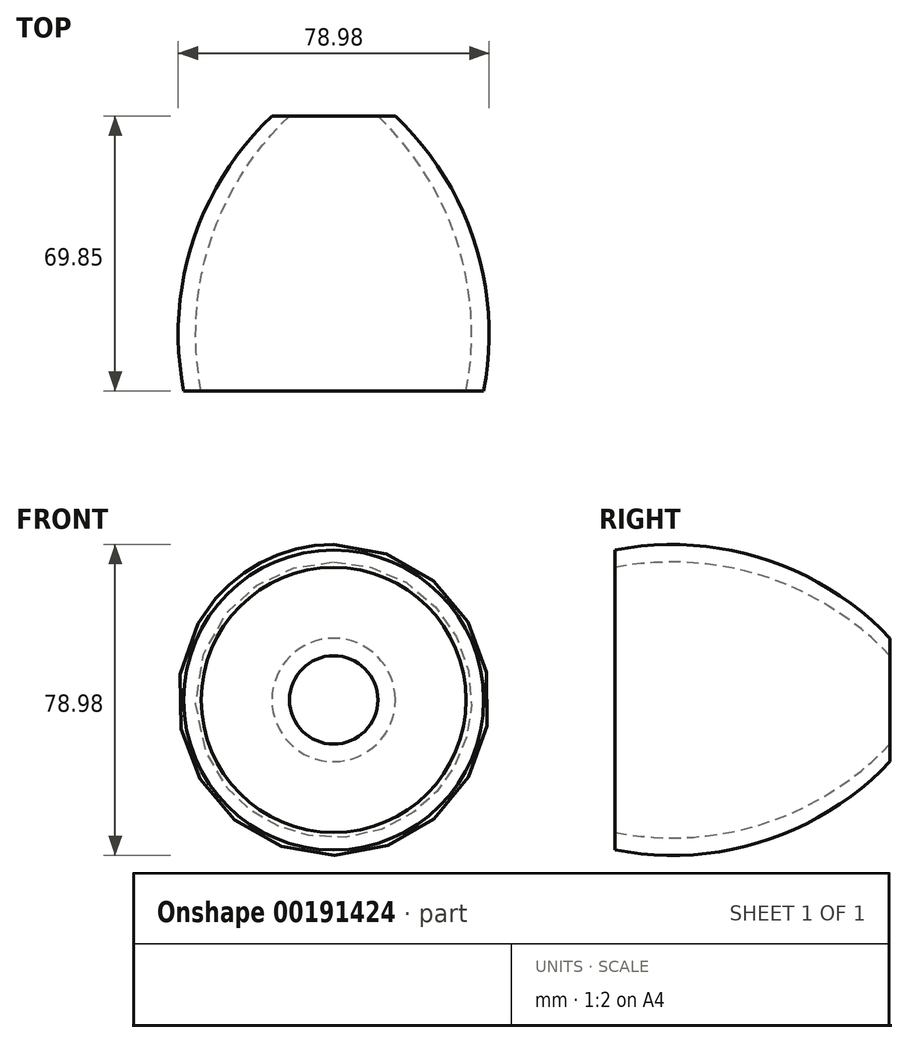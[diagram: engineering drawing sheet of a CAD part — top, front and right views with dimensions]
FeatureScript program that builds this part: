
annotation { "Feature Type Name" : "Feature", "Feature Type Description" : "" }
export const myFeature = defineFeature(function(context is Context, id is Id, definition is map)
    precondition{}
    {
        {
            var Q0;
            Q0=qCreatedBy(makeId("Top.planeOp"),FACE);
            var sketch = newSketch(context, id + "F0", { "sketchPlane" : qUnion([Q0])});
            skLineSegment(sketch, "E0", {"start": v(0, 0) * mm, "end": v(-38.1, 0) * mm});
            skArc(sketch, "E1", {"start": v(0, 81.28) * mm, "mid": v(-32.29, 46.85) * mm, "end": v(-38.1, 0) * mm});
            skLineSegment(sketch, "E2", {"start": v(0, 81.28) * mm, "end": v(0, 0) * mm});
            skLineSegment(sketch, "E3", {"start": v(0, 69.85) * mm, "end": v(-15.67, 69.85) * mm});
            skArc(sketch, "E4", {"start": v(-11.22, 69.85) * mm, "mid": v(-31.4, 37.8) * mm, "end": v(-33.66, 0) * mm});
            skSolve(sketch);
        }
        {
            var Q0;
            {var subQ3=sQuery(id+"F0.wireOp",EDGE,"E4");Q0=makeQuery(id+"F0.imprint","IMPRINT",FACE,{"disambiguationData":[TD([[makeQuery(id+"F0.imprint","IMPRINT",EDGE,{"derivedFrom":subQ3}),-1.0]])]});}
            var Q1;
            Q1=sQuery(id+"F0.wireOp",EDGE,"E2");
            revolve(context, id + "F1", {"entities" : qUnion([Q0]), "axis" : qUnion([Q1]), "revolveType" : RevolveType.FULL});
        }
    });
